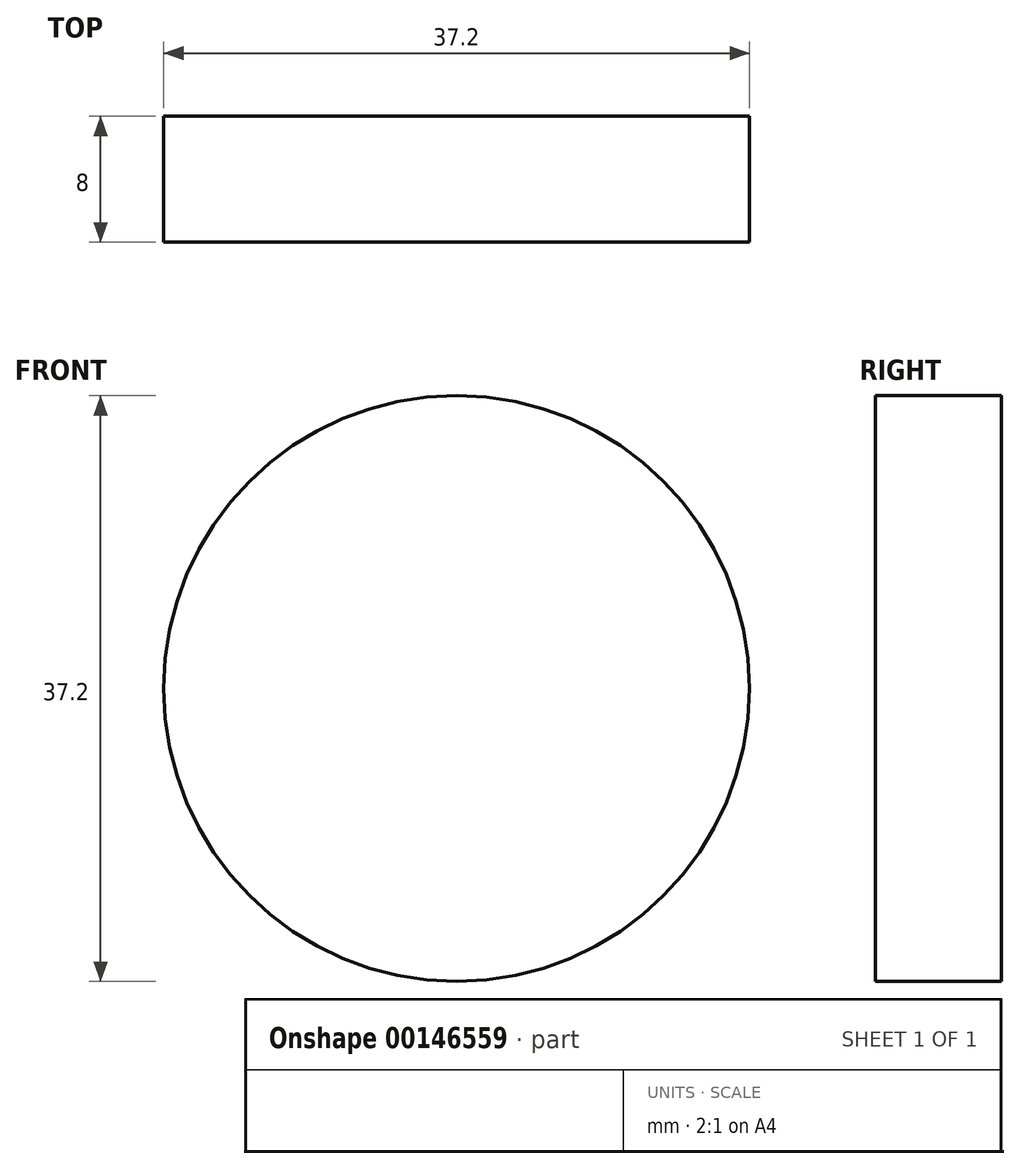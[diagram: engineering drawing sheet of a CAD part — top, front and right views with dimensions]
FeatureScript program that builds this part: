
annotation { "Feature Type Name" : "Feature", "Feature Type Description" : "" }
export const myFeature = defineFeature(function(context is Context, id is Id, definition is map)
    precondition{}
    {
        {
            var Q0;
            Q0=qCreatedBy(makeId("Front.planeOp"),FACE);
            var sketch = newSketch(context, id + "F0", { "sketchPlane" : qUnion([Q0])});
            skCircle(sketch, "E0", {"center": v(0, 0) * mm, "radius": 18.6 * mm});
            skSolve(sketch);
        }
        {
            var Q0;
            Q0=makeQuery(id+"F0.imprint","IMPRINT",FACE,{"disambiguationData":[TD([[makeQuery(id+"F0.imprint","IMPRINT",EDGE,{"derivedFrom":sQuery(id+"F0.wireOp",EDGE,"E0")}),1.0]])]});
            extrude(context, id + "F1", {"entities" : qUnion([Q0]), "depth" : 8 * mm, "symmetric" : true});
        }
    });
